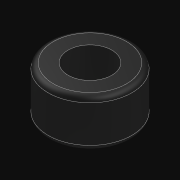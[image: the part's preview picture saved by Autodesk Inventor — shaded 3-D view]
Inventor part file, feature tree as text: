
AUTODESK INVENTOR PART (.ipt)
format: ipt  version: 2021.3 (Build 253353010, 353A)  size: 147,968 bytes
history: native  units: in
note: dims shown in document units (in); Inventor stores cm internally (conversion verified against a paired STEP export)
features: other x3, extrude x1, fillet x1, sketch x1
ambient origin geometry x8: Origin, YZ Plane, XZ Plane, XY Plane, X Axis, Y Axis, Z Axis, Center Point
bodies: Solid1 (feature_tree)
feature tree (6):
  other  "Table"
  other  "PSpacer 4.6"
  other  "PSpacer 8.0"
  extrude  "Extrusion1"  Depth=0.02in
  fillet  "Fillet1"  [1 undecoded]
  sketch  "Sketch1"  dims[d0=0.32in d1=0.167in d3=0.0in d4=0.02in]
note: 1 required parameter value undecoded (feature->parameter linkage not recoverable at this tier; creation-order binding heuristic only, values carry confidence <= 0.55)
